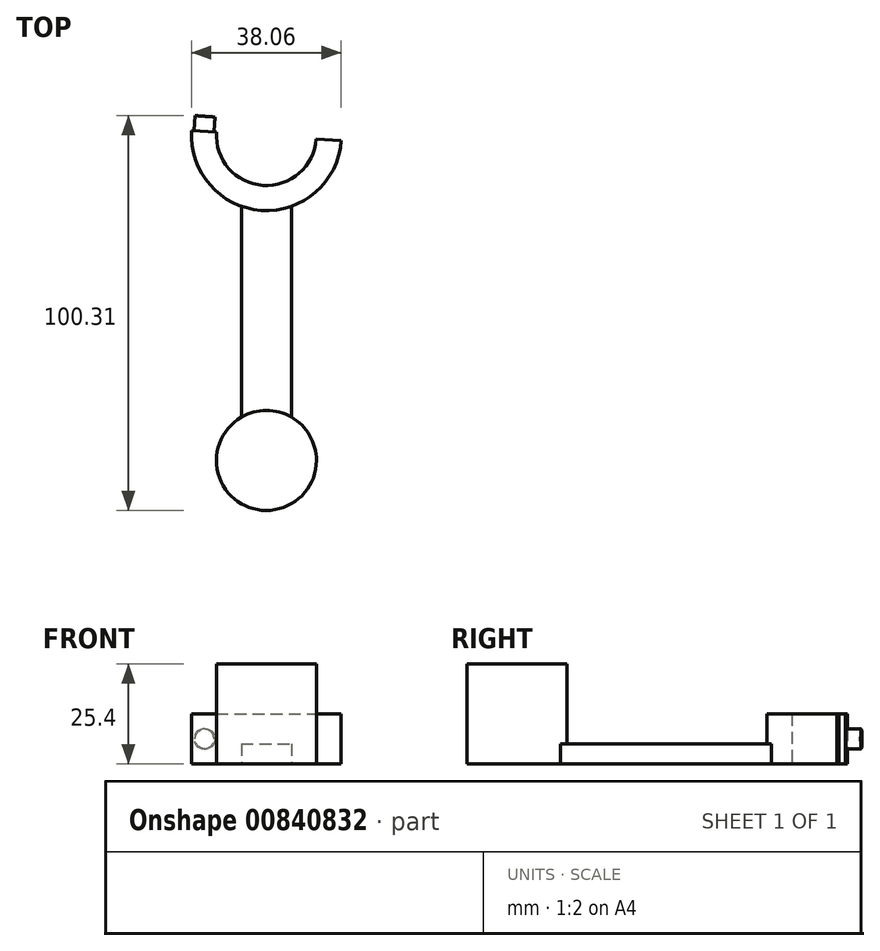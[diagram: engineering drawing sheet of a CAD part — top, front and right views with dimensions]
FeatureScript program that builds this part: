
annotation { "Feature Type Name" : "Feature", "Feature Type Description" : "" }
export const myFeature = defineFeature(function(context is Context, id is Id, definition is map)
    precondition{}
    {
        {
            var Q0;
            Q0=qCreatedBy(makeId("Top.planeOp"),FACE);
            var sketch = newSketch(context, id + "F0", { "sketchPlane" : qUnion([Q0])});
            skLineSegment(sketch, "E0.top", {"start": v(-12.7, -42.14) * mm, "end": v(0, -42.14) * mm});
            skLineSegment(sketch, "E0.left", {"start": v(-12.7, 34.06) * mm, "end": v(-12.7, -42.14) * mm});
            skLineSegment(sketch, "E0.right", {"start": v(0, 34.06) * mm, "end": v(0, -42.14) * mm});
            skLineSegment(sketch, "E1", {"start": v(0, -42.14) * mm, "end": v(-6.35, -42.14) * mm});
            skCircle(sketch, "E2", {"center": v(-6.35, -42.14) * mm, "radius": 12.7 * mm});
            skPoint(sketch, "E3.oppositeSnap0", {"position": v(-12.7, 40.4) * mm});
            skCircle(sketch, "E4", {"center": v(-6.35, 40.4) * mm, "radius": 12.7 * mm});
            skCircle(sketch, "E5", {"center": v(-6.35, 40.4) * mm, "radius": 19.05 * mm});
            skLineSegment(sketch, "E6", {"start": v(-6.35, 40.4) * mm, "end": v(-25.36, 41.7) * mm});
            skLineSegment(sketch, "E7", {"start": v(-6.35, 40.4) * mm, "end": v(12.66, 39.1) * mm});
            skLineSegment(sketch, "E8.bottom", {"start": v(-25.36, 41.7) * mm, "end": v(-19, 41.7) * mm});
            skLineSegment(sketch, "E8.top", {"start": v(-25.36, 49.33) * mm, "end": v(-19, 49.33) * mm});
            skLineSegment(sketch, "E8.left", {"start": v(-25.36, 41.7) * mm, "end": v(-25.36, 49.33) * mm});
            skLineSegment(sketch, "E8.right", {"start": v(-19, 41.7) * mm, "end": v(-19, 49.33) * mm});
            skSolve(sketch);
        }
        {
            var Q0;
            {var subQ0=sQuery(id+"F0.wireOp",EDGE,"E5");var subQ1=sQuery(id+"F0.wireOp",EDGE,"E0.left");var subQ2=makeQuery(id+"F0.imprint","INTERSECT",VERTEX,{"derivedFrom":[subQ1,subQ0]});Q0=makeQuery(id+"F0.imprint","IMPRINT",FACE,{"disambiguationData":[TD([[makeQuery(id+"F0.imprint","IMPRINT",EDGE,{"disambiguationData":[TD([[subQ2,1.0]])],"derivedFrom":subQ1}),1.0]])]});}
            var Q1;
            {var subQ0=sQuery(id+"F0.wireOp",EDGE,"E5");var subQ1=sQuery(id+"F0.wireOp",EDGE,"E0.left");var subQ2=makeQuery(id+"F0.imprint","INTERSECT",VERTEX,{"derivedFrom":[subQ1,subQ0]});Q1=makeQuery(id+"F0.imprint","IMPRINT",FACE,{"disambiguationData":[TD([[makeQuery(id+"F0.imprint","IMPRINT",EDGE,{"disambiguationData":[TD([[subQ2,1.0]])],"derivedFrom":subQ1}),-1.0]])]});}
            var Q2;
            {var subQ0=sQuery(id+"F0.wireOp",EDGE,"E5");var subQ1=sQuery(id+"F0.wireOp",EDGE,"E0.right");var subQ2=makeQuery(id+"F0.imprint","INTERSECT",VERTEX,{"derivedFrom":[subQ1,subQ0]});Q2=makeQuery(id+"F0.imprint","IMPRINT",FACE,{"disambiguationData":[TD([[makeQuery(id+"F0.imprint","IMPRINT",EDGE,{"disambiguationData":[TD([[subQ2,1.0]])],"derivedFrom":subQ1}),1.0]])]});}
            extrude(context, id + "F1", {"entities" : qUnion([Q0, Q1, Q2]), "depth" : 12.7 * mm, "offsetDistance" : 25.4 * mm});
        }
        {
            var Q0;
            {var subQ0=sQuery(id+"F0.wireOp",EDGE,"E5");var subQ1=sQuery(id+"F0.wireOp",EDGE,"E0.left");var subQ2=makeQuery(id+"F0.imprint","INTERSECT",VERTEX,{"derivedFrom":[subQ1,subQ0]});Q0=makeQuery(id+"F0.imprint","IMPRINT",FACE,{"disambiguationData":[TD([[makeQuery(id+"F0.imprint","IMPRINT",EDGE,{"disambiguationData":[TD([[subQ2,-1.0]])],"derivedFrom":subQ1}),1.0]])]});}
            extrude(context, id + "F2", {"entities" : qUnion([Q0]), "operationType" : NewBodyOperationType.ADD, "depth" : 5.08 * mm, "offsetDistance" : 25.4 * mm});
        }
        {
            var Q0;
            {var subQ5=sQuery(id+"F0.wireOp",EDGE,"E0.top");Q0=makeQuery(id+"F0.imprint","IMPRINT",FACE,{"disambiguationData":[TD([[makeQuery(id+"F0.imprint","IMPRINT",EDGE,{"derivedFrom":subQ5}),1.0]])]});}
            var Q1;
            {var subQ5=sQuery(id+"F0.wireOp",EDGE,"E0.top");Q1=makeQuery(id+"F0.imprint","IMPRINT",FACE,{"disambiguationData":[TD([[makeQuery(id+"F0.imprint","IMPRINT",EDGE,{"derivedFrom":subQ5}),-1.0]])]});}
            extrude(context, id + "F3", {"entities" : qUnion([Q0, Q1]), "operationType" : NewBodyOperationType.ADD, "depth" : 25.4 * mm, "offsetDistance" : 25.4 * mm});
        }
        {
            var Q0;
            Q0=makeQuery(id+"F1.opExtrude","SWEPT_FACE",FACE,{"disambiguationData":[OSD([sQuery(id+"F0.wireOp",EDGE,"E6")])]});
            var sketch = newSketch(context, id + "F4", { "sketchPlane" : qUnion([Q0])});
            skLineSegment(sketch, "E9.bottom", {"start": v(28.14, 0) * mm, "end": v(24.97, 0) * mm});
            skLineSegment(sketch, "E9.left", {"start": v(28.14, 0) * mm, "end": v(28.14, 6.35) * mm});
            skLineSegment(sketch, "E10.bottom", {"start": v(24.97, 0) * mm, "end": v(28.14, 0) * mm});
            skCircle(sketch, "E11", {"center": v(24.97, 6.35) * mm, "radius": 2.54 * mm});
            skSolve(sketch);
        }
        {
            var Q0;
            Q0=makeQuery(id+"F4.imprint","IMPRINT",FACE,{"disambiguationData":[TD([[makeQuery(id+"F4.imprint","IMPRINT",EDGE,{"derivedFrom":sQuery(id+"F4.wireOp",EDGE,"E11")}),1.0]])]});
            extrude(context, id + "F5", {"entities" : qUnion([Q0]), "operationType" : NewBodyOperationType.ADD, "depth" : 3.8 * mm, "offsetDistance" : 25.4 * mm});
        }
    });
